# Revit family: AD-C6T
name_source: partatom
category: Communication Devices
revit_build: Autodesk Revit 2014 (Build: 20130308_1515(x64)
units: mm (PartAtom-declared; Revit-internal decimal feet)

## types (1)
- AD-C6T
    100V Taps = 15, 30, 60
    70V Taps = 7.5, 15, 30, 60
    Coverage Horizontal = 105.00°
    Coverage Vertical = 105.00°
    Default Elevation = 0 mm
    Depth = 237 mm
    Description = 6.5" Two-way Loudspeaker
    Enclosure Depth = 215 mm
    Enclosure Radius = 114 mm
    Grille Depth = 5 mm
    Grille Radius Base = 140 mm
    Grille Radius Extent = 120 mm
    Impedance = 16
    Manufacturer = QSC Audio Products, LLC
    Manufacturer URL = www.qscaudio.com
    Middle Depth = 17 mm
    Middle Radius = 120 mm
    Model = AD-C6T
    Power Handling = 120
    Regulatory Compliance = EN54-24, UL1480, UL2043, NFPA90, NFPA70, UL1876, ROHS, C-TICK X000, CE
    SPL Max = 113.9
    Sensitivity = 90.1
    Weight Dimensional (kg) = 6.3
    Weight Dimensional (lb) = 13.9
    Weight Product (kg) = 4.3
    Weight Product (lb) = 9.5
    Width = 280 mm

## geometry (parser evidence)
native form markers: Blend x11, Sweep x1
no freeform markers — native parametric forms only
